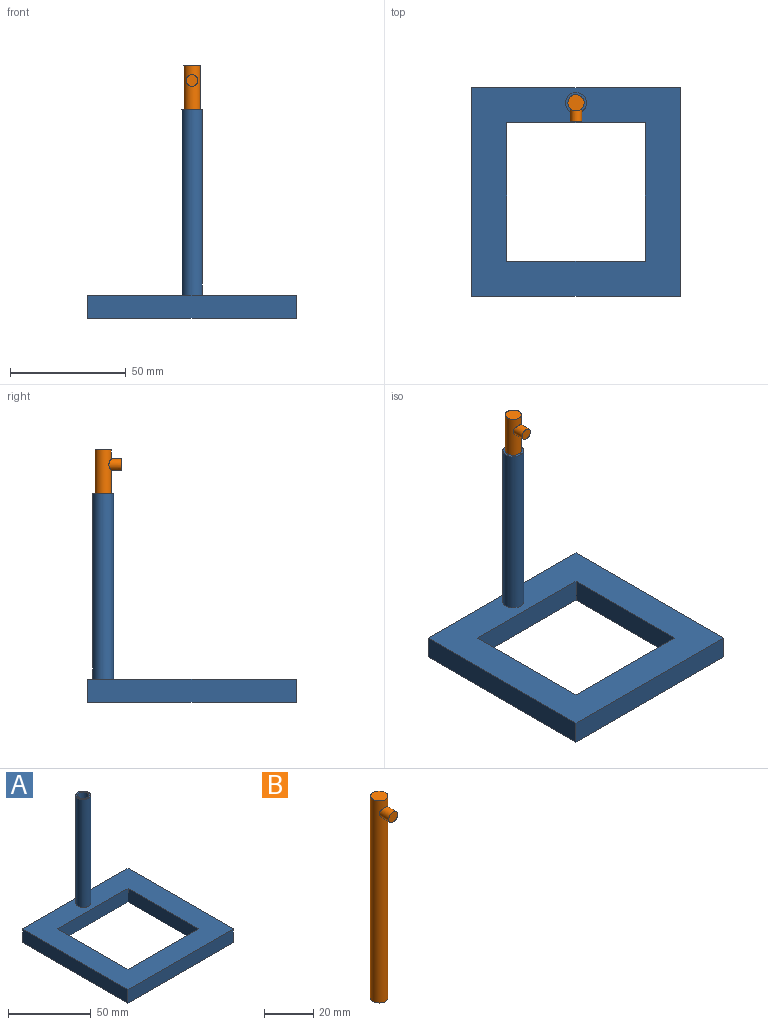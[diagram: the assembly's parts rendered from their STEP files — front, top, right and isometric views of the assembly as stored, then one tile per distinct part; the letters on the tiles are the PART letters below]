
ASSEMBLY  parts=2 mates=1
PART A: 23 faces, bbox 90x90x90 mm
  f0: plane 90x10mm, normal (0,1,0), area 900mm2, adj f1,f3,f4,f5
  f1: plane 90x10mm, normal (-1,0,0), area 900mm2, adj f0,f2,f4,f5
  f2: plane 90x10mm, normal (0,-1,0), area 900mm2, adj f1,f3,f4,f5
  f3: plane 90x10mm, normal (1,0,0), area 900mm2, adj f0,f2,f4,f5
  f4: plane 90x90mm, normal (0,0,1), area 4436.4mm2, adj f0,f1,f2,f3,f6,f7,f8,f9
  f5: plane 90x90mm, normal (0,0,-1), area 4500mm2, adj f0,f1,f2,f3,f6,f7,f8,f9
  f6: plane 60x10mm, normal (1,0,0), area 600mm2, adj f4,f5,f7,f9
  f7: plane 60x10mm, normal (0,1,0), area 600mm2, adj f4,f5,f6,f8
  f8: plane 60x10mm, normal (-1,0,0), area 600mm2, adj f4,f5,f7,f9
  f9: plane 60x10mm, normal (0,-1,0), area 600mm2, adj f4,f5,f6,f8
  f10: cylinder r=4.5mm len=80mm, axis (0,0,-1), area 2261.9mm2, adj f4,f11
  f11: plane 9x9mm, normal (0,0,1), area 25.1mm2, adj f10,f22
  f12: plane 88x8mm, normal (0,-1,0), area 704mm2, adj f13,f15,f16,f17
  f13: plane 88x8mm, normal (1,0,0), area 704mm2, adj f12,f14,f16,f17
  f14: plane 88x8mm, normal (0,1,0), area 704mm2, adj f13,f15,f16,f17
  f15: plane 88x8mm, normal (-1,0,0), area 704mm2, adj f12,f14,f16,f17
  f16: plane 88x88mm, normal (0,0,-1), area 3861.5mm2, adj f12,f13,f14,f15,f18,f19,f20,f21
  f17: plane 88x88mm, normal (0,0,1), area 3900mm2, adj f12,f13,f14,f15,f18,f19,f20,f21
  f18: plane 62x8mm, normal (-1,0,0), area 496mm2, adj f16,f17,f19,f21
  f19: plane 62x8mm, normal (0,-1,0), area 496mm2, adj f16,f17,f18,f20
  f20: plane 62x8mm, normal (1,0,0), area 496mm2, adj f16,f17,f19,f21
  f21: plane 62x8mm, normal (0,1,0), area 496mm2, adj f16,f17,f18,f20
  f22: cylinder r=3.5mm len=81mm, axis (0,0,-1), area 1781.3mm2, adj f11,f16
PART B: 5 faces, bbox 7x11.5x100 mm
  f0: cylinder r=3.5mm len=100mm, axis (0,0,-1), area 2177.9mm2, adj f1,f2,f3
  f1: plane 7x7mm, normal (0,0,1), area 38.5mm2, adj f0
  f2: plane 7x7mm, normal (0,0,-1), area 38.5mm2, adj f0
  f3: cylinder r=2.5mm len=5.55mm, axis (0,1,0), area 78.6mm2, adj f0,f4
  f4: plane 5x5mm, normal (0,-1,0), area 19.6mm2, adj f3
PLACE A t=(-102.97,-34.6,-16.1)mm
PLACE B t=(-102.97,3.77,-7.1)mm
MATE slider B.f0 <-> A.f10  axis (0,0,-1) through (-102.97,3.77,-7.1)mm
